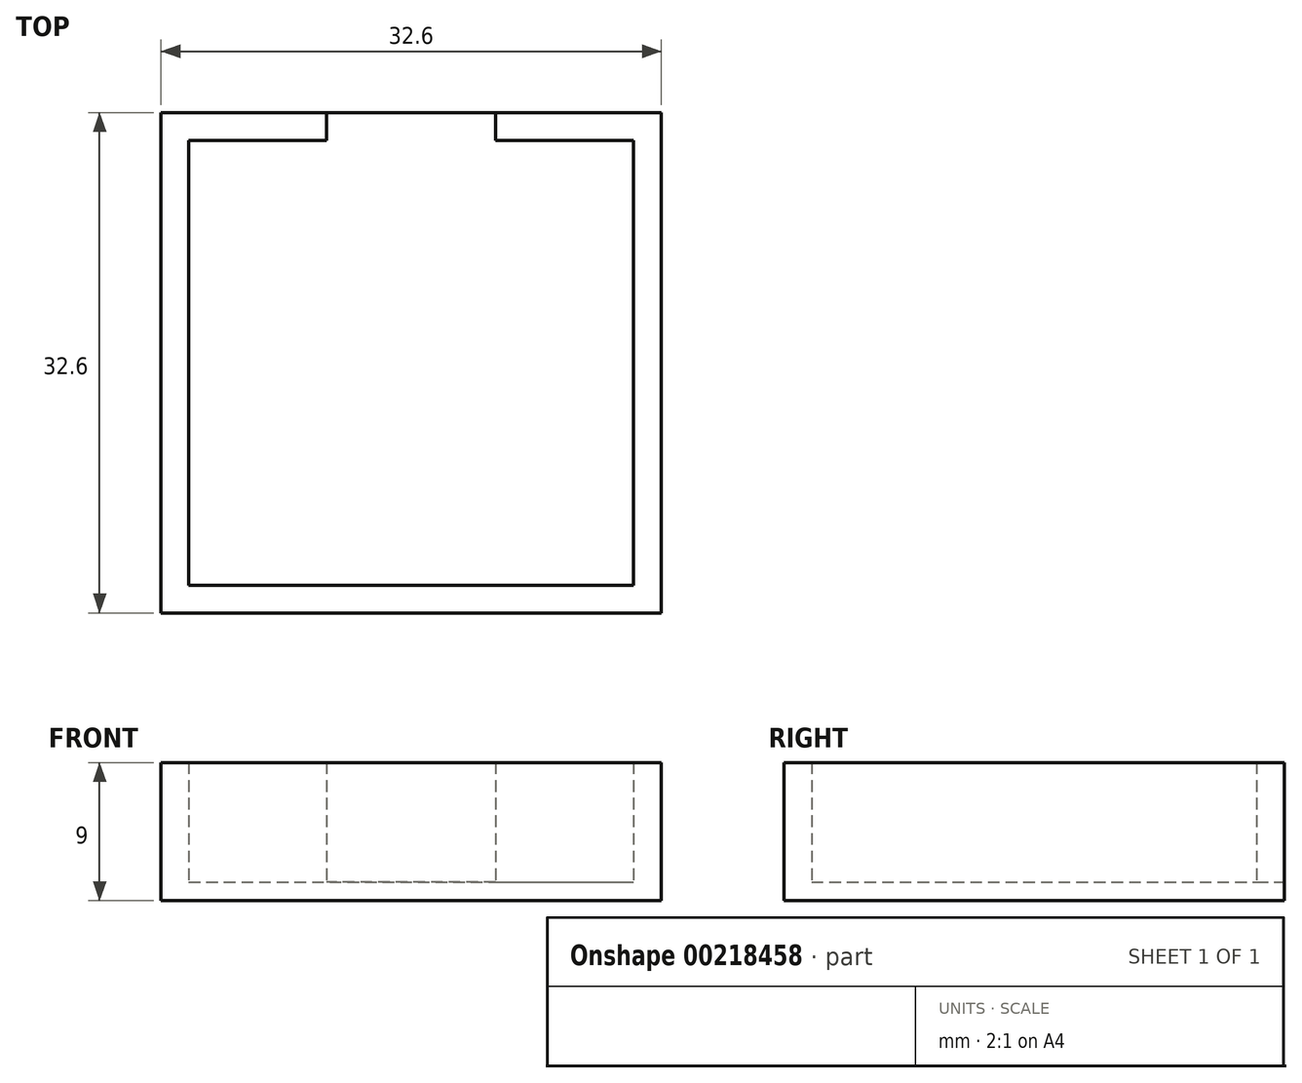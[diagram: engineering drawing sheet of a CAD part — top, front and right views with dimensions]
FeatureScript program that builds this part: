
annotation { "Feature Type Name" : "Feature", "Feature Type Description" : "" }
export const myFeature = defineFeature(function(context is Context, id is Id, definition is map)
    precondition{}
    {
        {
            var Q0;
            Q0=qCreatedBy(makeId("Top.planeOp"),FACE);
            var sketch = newSketch(context, id + "F0", { "sketchPlane" : qUnion([Q0])});
            skLineSegment(sketch, "E0.bottom", {"start": v(14.5, 14.5) * mm, "end": v(-14.5, 14.5) * mm});
            skLineSegment(sketch, "E0.top", {"start": v(14.5, -14.5) * mm, "end": v(-14.5, -14.5) * mm});
            skLineSegment(sketch, "E0.left", {"start": v(14.5, 14.5) * mm, "end": v(14.5, -14.5) * mm});
            skLineSegment(sketch, "E0.right", {"start": v(-14.5, 14.5) * mm, "end": v(-14.5, -14.5) * mm});
            skPoint(sketch, "E0.middle", {"position": v(0, 0) * mm});
            skLineSegment(sketch, "E1.0", {"start": v(-16.3, 16.3) * mm, "end": v(-16.3, -16.3) * mm});
            skLineSegment(sketch, "E1.1", {"start": v(16.3, 16.3) * mm, "end": v(-16.3, 16.3) * mm});
            skLineSegment(sketch, "E1.2", {"start": v(16.3, 16.3) * mm, "end": v(16.3, -16.3) * mm});
            skLineSegment(sketch, "E1.3", {"start": v(16.3, -16.3) * mm, "end": v(-16.3, -16.3) * mm});
            skLineSegment(sketch, "E2.bottom", {"start": v(5.5, 16.3) * mm, "end": v(-5.5, 16.3) * mm});
            skLineSegment(sketch, "E2.left", {"start": v(5.5, 16.3) * mm, "end": v(5.5, 14.5) * mm});
            skLineSegment(sketch, "E2.right", {"start": v(-5.5, 16.3) * mm, "end": v(-5.5, 14.5) * mm});
            skPoint(sketch, "E2.middle", {"position": v(0, 14.5) * mm});
            skPoint(sketch, "E3.orphan", {"position": v(5.5, 12.7) * mm});
            skPoint(sketch, "E4.orphan", {"position": v(-5.5, 12.7) * mm});
            skSolve(sketch);
        }
        {
            var Q0;
            Q0=qSketchRegion(id+"F0",true);
            var Q1;
            Q1=makeQuery(id+"F0.imprint","IMPRINT",FACE,{"disambiguationData":[TD([[makeQuery(id+"F0.imprint","IMPRINT",EDGE,{"derivedFrom":sQuery(id+"F0.wireOp",EDGE,"E0.top")}),-1.0]])]});
            extrude(context, id + "F1", {"entities" : qUnion([Q0, Q1]), "depth" : 1.2 * mm});
        }
        {
            var Q0;
            Q0=makeQuery(id+"F0.imprint","IMPRINT",FACE,{"disambiguationData":[TD([[makeQuery(id+"F0.imprint","IMPRINT",EDGE,{"derivedFrom":sQuery(id+"F0.wireOp",EDGE,"E0.top")}),1.0]])]});
            var Q1;
            Q1=makeQuery(id+"F0.imprint","IMPRINT",FACE,{"disambiguationData":[TD([[makeQuery(id+"F0.imprint","IMPRINT",EDGE,{"derivedFrom":sQuery(id+"F0.wireOp",EDGE,"E2.bottom")}),1.0]])]});
            extrude(context, id + "F2", {"entities" : qUnion([Q0, Q1]), "operationType" : NewBodyOperationType.ADD, "depth" : 9 * mm});
        }
    });
